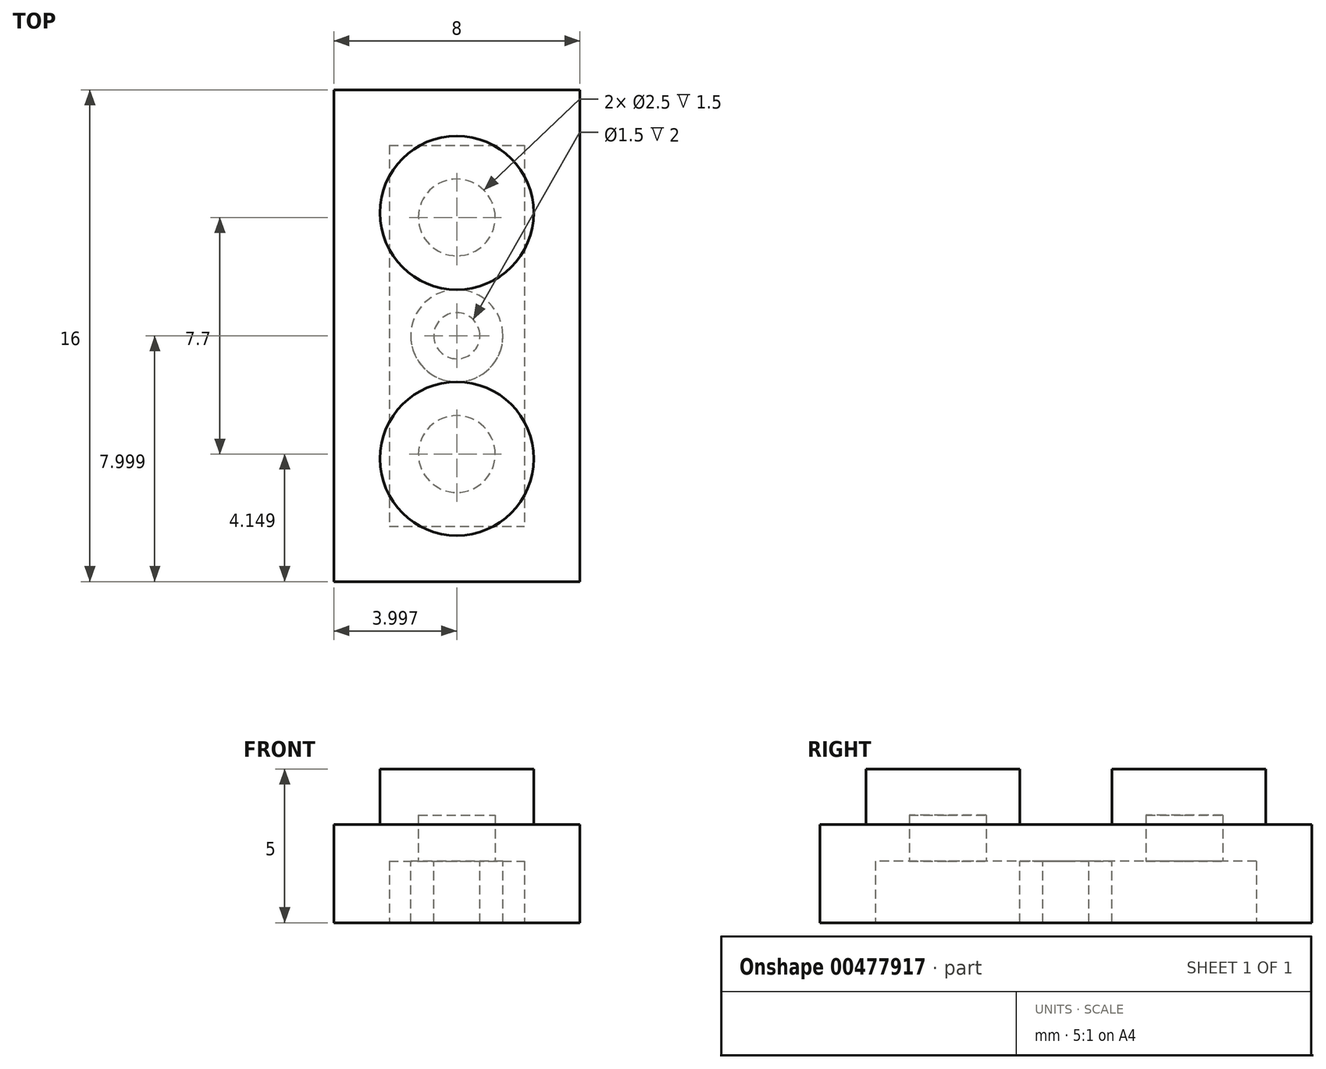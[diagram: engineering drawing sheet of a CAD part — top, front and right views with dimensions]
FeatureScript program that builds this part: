
annotation { "Feature Type Name" : "Feature", "Feature Type Description" : "" }
export const myFeature = defineFeature(function(context is Context, id is Id, definition is map)
    precondition{}
    {
        {
            var Q0;
            Q0=qCreatedBy(makeId("Top.planeOp"),FACE);
            var sketch = newSketch(context, id + "F0", { "sketchPlane" : qUnion([Q0])});
            skLineSegment(sketch, "E0.bottom", {"start": v(-2.22, -5.52) * mm, "end": v(5.78, -5.52) * mm});
            skLineSegment(sketch, "E0.top", {"start": v(-2.22, -21.52) * mm, "end": v(5.78, -21.52) * mm});
            skLineSegment(sketch, "E0.left", {"start": v(-2.22, -5.52) * mm, "end": v(-2.22, -21.52) * mm});
            skLineSegment(sketch, "E0.right", {"start": v(5.78, -5.52) * mm, "end": v(5.78, -21.52) * mm});
            skLineSegment(sketch, "E1.0", {"start": v(-0.42, -7.32) * mm, "end": v(-0.42, -19.72) * mm});
            skLineSegment(sketch, "E1.1", {"start": v(-0.42, -7.32) * mm, "end": v(3.98, -7.32) * mm});
            skLineSegment(sketch, "E1.2", {"start": v(3.98, -7.32) * mm, "end": v(3.98, -19.72) * mm});
            skLineSegment(sketch, "E1.3", {"start": v(-0.42, -19.72) * mm, "end": v(3.98, -19.72) * mm});
            skSolve(sketch);
        }
        {
            var Q0;
            Q0=makeQuery(id+"F0.imprint","IMPRINT",FACE,{"disambiguationData":[TD([[makeQuery(id+"F0.imprint","IMPRINT",EDGE,{"derivedFrom":sQuery(id+"F0.wireOp",EDGE,"E0.bottom")}),-1.0]])]});
            extrude(context, id + "F1", {"entities" : qUnion([Q0]), "depth" : 2 * mm});
        }
        {
            var Q0;
            Q0=makeQuery(id+"F1.opExtrude","CAP_FACE",FACE,{"disambiguationData":[OSD([sQuery(id+"F0.wireOp",EDGE,"E0.bottom"),sQuery(id+"F0.wireOp",EDGE,"E0.top"),sQuery(id+"F0.wireOp",EDGE,"E0.left"),sQuery(id+"F0.wireOp",EDGE,"E0.right"),sQuery(id+"F0.wireOp",EDGE,"E1.0"),sQuery(id+"F0.wireOp",EDGE,"E1.1"),sQuery(id+"F0.wireOp",EDGE,"E1.2"),sQuery(id+"F0.wireOp",EDGE,"E1.3")])],"isStart":false});
            var sketch = newSketch(context, id + "F2", { "sketchPlane" : qUnion([Q0])});
            skLineSegment(sketch, "E2.bottom", {"start": v(-2.22, -5.52) * mm, "end": v(5.78, -5.52) * mm});
            skLineSegment(sketch, "E2.top", {"start": v(-2.22, -21.52) * mm, "end": v(5.78, -21.52) * mm});
            skLineSegment(sketch, "E2.left", {"start": v(-2.22, -5.52) * mm, "end": v(-2.22, -21.52) * mm});
            skLineSegment(sketch, "E2.right", {"start": v(5.78, -5.52) * mm, "end": v(5.78, -21.52) * mm});
            skSolve(sketch);
        }
        {
            var Q0;
            Q0 = qSketchRegion(id + "F2", true);
            extrude(context, id + "F3", {"entities" : qUnion([Q0]), "operationType" : NewBodyOperationType.ADD, "depth" : 1.2 * mm});
        }
        {
            var Q0;
            Q0=makeQuery(id+"F3.opExtrude","CAP_FACE",FACE,{"disambiguationData":[OSD([sQuery(id+"F2.wireOp",EDGE,"E2.bottom"),sQuery(id+"F2.wireOp",EDGE,"E2.top"),sQuery(id+"F2.wireOp",EDGE,"E2.left"),sQuery(id+"F2.wireOp",EDGE,"E2.right")])],"isStart":false});
            var sketch = newSketch(context, id + "F4", { "sketchPlane" : qUnion([Q0])});
            skCircle(sketch, "E3", {"center": v(1.78, -9.52) * mm, "radius": 2.5 * mm});
            skCircle(sketch, "E4", {"center": v(1.78, -17.52) * mm, "radius": 2.5 * mm});
            skSolve(sketch);
        }
        {
            var Q0;
            Q0=makeQuery(id+"F4.imprint","IMPRINT",FACE,{"disambiguationData":[TD([[makeQuery(id+"F4.imprint","IMPRINT",EDGE,{"derivedFrom":sQuery(id+"F4.wireOp",EDGE,"E3")}),1.0]])]});
            var Q1;
            Q1=makeQuery(id+"F4.imprint","IMPRINT",FACE,{"disambiguationData":[TD([[makeQuery(id+"F4.imprint","IMPRINT",EDGE,{"derivedFrom":sQuery(id+"F4.wireOp",EDGE,"E4")}),1.0]])]});
            extrude(context, id + "F5", {"entities" : qUnion([Q0, Q1]), "operationType" : NewBodyOperationType.ADD, "depth" : 1.8 * mm});
        }
        {
            var Q0;
            Q0=makeQuery(id+"F3.opExtrude","CAP_FACE",FACE,{"disambiguationData":[OSD([sQuery(id+"F2.wireOp",EDGE,"E2.bottom"),sQuery(id+"F2.wireOp",EDGE,"E2.top"),sQuery(id+"F2.wireOp",EDGE,"E2.left"),sQuery(id+"F2.wireOp",EDGE,"E2.right")])],"isStart":true});
            var sketch = newSketch(context, id + "F6", { "sketchPlane" : qUnion([Q0])});
            skLineSegment(sketch, "E5", {"start": v(-0.42, 13.52) * mm, "end": v(3.98, 13.52) * mm});
            skCircle(sketch, "E6", {"center": v(1.78, 13.52) * mm, "radius": 1.5 * mm});
            skCircle(sketch, "E7", {"center": v(1.78, 13.52) * mm, "radius": 0.75 * mm});
            skSolve(sketch);
        }
        {
            var Q0;
            Q0 = qSketchRegion(id + "F6", true);
            extrude(context, id + "F7", {"entities" : qUnion([Q0]), "operationType" : NewBodyOperationType.ADD, "depth" : 2 * mm});
        }
        {
            var Q0;
            Q0=makeQuery(id+"F7.boolean.opBoolean","SPLIT",FACE,{"disambiguationData":[TD([makeQuery(id+"F1.opExtrude","SWEPT_FACE",FACE,{"disambiguationData":[OSD([sQuery(id+"F0.wireOp",EDGE,"E1.0")])]})])],"derivedFrom":makeQuery(id+"F3.opExtrude","CAP_FACE",FACE,{"disambiguationData":[OSD([sQuery(id+"F2.wireOp",EDGE,"E2.bottom"),sQuery(id+"F2.wireOp",EDGE,"E2.top"),sQuery(id+"F2.wireOp",EDGE,"E2.left"),sQuery(id+"F2.wireOp",EDGE,"E2.right")])],"isStart":true})});
            var sketch = newSketch(context, id + "F8", { "sketchPlane" : qUnion([Q0])});
            skCircle(sketch, "E8", {"center": v(1.78, 17.37) * mm, "radius": 1.25 * mm});
            skCircle(sketch, "E9", {"center": v(1.78, 9.67) * mm, "radius": 1.25 * mm});
            skSolve(sketch);
        }
        {
            var Q0;
            Q0 = qSketchRegion(id + "F8", true);
            extrude(context, id + "F9", {"entities" : qUnion([Q0]), "operationType" : NewBodyOperationType.REMOVE, "oppositeDirection" : true, "depth" : 1.5 * mm});
        }
    });
